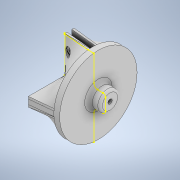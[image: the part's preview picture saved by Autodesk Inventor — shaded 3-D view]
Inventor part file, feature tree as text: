
AUTODESK INVENTOR PART (.ipt)
format: ipt  version: 2022 (Build 260153000, 153)  size: 528,384 bytes
history: native  units: mm
features: other x6, sketch x6, extrude x5, projected_geometry x5, pattern_circular x1, fillet x1
ambient origin geometry x8: Origin, YZ Plane, XZ Plane, XY Plane, X Axis, Y Axis, Z Axis, Center Point
bodies: Body1 (feature_tree), Body2 (feature_tree)
feature tree (24):
  other  "Твердое тело2"
  other  "Исправленная геометрия1"
  other  "РабПлоскость1"
  extrude  "Выдавливание1"  [1 undecoded]
  other  "РабПлоскость2"
  extrude  "Выдавливание2"  Depth=22.5mm
  extrude  "Выдавливание3"  Depth=17.5mm
  pattern_circular  "Круговой массив1"  [2 undecoded]
  other  "РабПлоскость3"
  extrude  "Выдавливание4"  Depth=20.0mm
  fillet  "Сопряжение2"  Radius=12.0mm
  extrude  "Выдавливание5"  [1 undecoded]
  sketch  "Эскиз8"
  sketch  "Эскиз1"
  sketch  "Эскиз2"
  projected_geometry  "Спроецированная петля1"
  projected_geometry  "Спроецированная петля2"
  sketch  "Эскиз3"
  projected_geometry  "Спроецированная петля3"
  projected_geometry  "Спроецированная петля4"
  sketch  "Эскиз4"
  sketch  "Эскиз5"
  projected_geometry  "Спроецированная петля5"
  other  "Твердое тело1"
note: 4 required parameter values undecoded (feature->parameter linkage not recoverable at this tier; creation-order binding heuristic only, values carry confidence <= 0.55)
